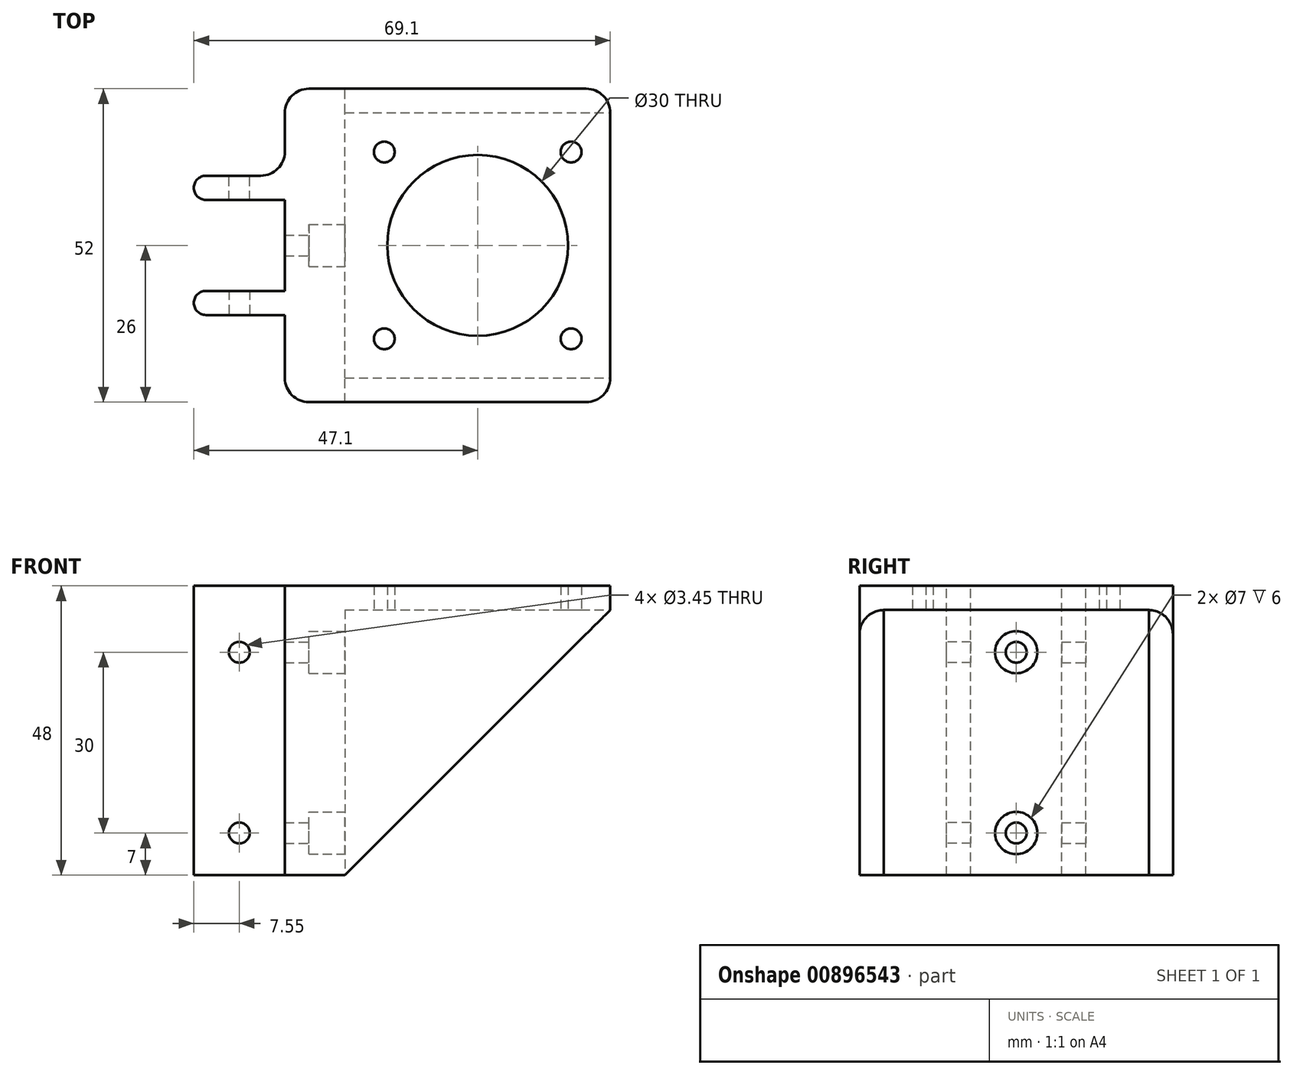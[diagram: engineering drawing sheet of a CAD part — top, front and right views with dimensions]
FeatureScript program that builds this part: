
annotation { "Feature Type Name" : "Feature", "Feature Type Description" : "" }
export const myFeature = defineFeature(function(context is Context, id is Id, definition is map)
    precondition{}
    {
        {
            var Q0;
            Q0=qCreatedBy(makeId("Top.planeOp"),FACE);
            var sketch = newSketch(context, id + "F0", { "sketchPlane" : qUnion([Q0])});
            skLineSegment(sketch, "E0.bottom", {"start": v(0, 0) * mm, "end": v(10, 0) * mm});
            skLineSegment(sketch, "E0.top", {"start": v(0, 52) * mm, "end": v(10, 52) * mm});
            skLineSegment(sketch, "E0.left", {"start": v(0, 0) * mm, "end": v(0, 52) * mm});
            skLineSegment(sketch, "E0.right", {"start": v(10, 0) * mm, "end": v(10, 52) * mm});
            skSolve(sketch);
        }
        {
            var Q0;
            Q0=qSketchRegion(id+"F0",true);
            extrude(context, id + "F1", {"entities" : qUnion([Q0]), "depth" : 44 * mm, "offsetDistance" : 25 * mm});
        }
        {
            var Q0;
            Q0=makeQuery(id+"F1.opExtrude","CAP_FACE",FACE,{"disambiguationData":[OSD([sQuery(id+"F0.wireOp",EDGE,"E0.bottom"),sQuery(id+"F0.wireOp",EDGE,"E0.top"),sQuery(id+"F0.wireOp",EDGE,"E0.left"),sQuery(id+"F0.wireOp",EDGE,"E0.right")])],"isStart":false});
            var sketch = newSketch(context, id + "F2", { "sketchPlane" : qUnion([Q0])});
            skLineSegment(sketch, "E1.bottom", {"start": v(0, 52) * mm, "end": v(54, 52) * mm});
            skLineSegment(sketch, "E1.top", {"start": v(0, 0) * mm, "end": v(54, 0) * mm});
            skLineSegment(sketch, "E1.left", {"start": v(0, 52) * mm, "end": v(0, 0) * mm});
            skLineSegment(sketch, "E1.right", {"start": v(54, 52) * mm, "end": v(54, 0) * mm});
            skSolve(sketch);
        }
        {
            var Q0;
            Q0=qSketchRegion(id+"F2",true);
            extrude(context, id + "F3", {"entities" : qUnion([Q0]), "operationType" : NewBodyOperationType.ADD, "depth" : 4 * mm, "offsetDistance" : 25 * mm});
        }
        {
            var Q0;
            Q0=makeQuery(id+"F3.boolean.opBoolean","MERGE",FACE,{"derivedFrom":[makeQuery(id+"F1.opExtrude","SWEPT_FACE",FACE,{"disambiguationData":[OSD([sQuery(id+"F0.wireOp",EDGE,"E0.bottom")])]}),makeQuery(id+"F3.opExtrude","SWEPT_FACE",FACE,{"disambiguationData":[OSD([sQuery(id+"F2.wireOp",EDGE,"E1.top")])]})]});
            var sketch = newSketch(context, id + "F4", { "sketchPlane" : qUnion([Q0])});
            skLineSegment(sketch, "E2", {"start": v(54, 44) * mm, "end": v(10, 0) * mm});
            skLineSegment(sketch, "E3", {"start": v(54, 44) * mm, "end": v(10, 44) * mm});
            skLineSegment(sketch, "E4", {"start": v(10, 44) * mm, "end": v(10, 0) * mm});
            skSolve(sketch);
        }
        {
            var Q0;
            Q0=qSketchRegion(id+"F4",true);
            extrude(context, id + "F5", {"entities" : qUnion([Q0]), "operationType" : NewBodyOperationType.ADD, "oppositeDirection" : true, "depth" : 4 * mm, "offsetDistance" : 25 * mm});
        }
        {
            var Q0;
            Q0=makeQuery(id+"F3.boolean.opBoolean","MERGE",FACE,{"derivedFrom":[makeQuery(id+"F1.opExtrude","SWEPT_FACE",FACE,{"disambiguationData":[OSD([sQuery(id+"F0.wireOp",EDGE,"E0.top")])]}),makeQuery(id+"F3.opExtrude","SWEPT_FACE",FACE,{"disambiguationData":[OSD([sQuery(id+"F2.wireOp",EDGE,"E1.bottom")])]})]});
            var sketch = newSketch(context, id + "F6", { "sketchPlane" : qUnion([Q0])});
            skLineSegment(sketch, "E5", {"start": v(-54, 44) * mm, "end": v(-10, 0) * mm});
            skLineSegment(sketch, "E6", {"start": v(-10, 0) * mm, "end": v(-10, 44) * mm});
            skLineSegment(sketch, "E7", {"start": v(-10, 44) * mm, "end": v(-54, 44) * mm});
            skSolve(sketch);
        }
        {
            var Q0;
            Q0=qSketchRegion(id+"F6",true);
            extrude(context, id + "F7", {"entities" : qUnion([Q0]), "operationType" : NewBodyOperationType.ADD, "oppositeDirection" : true, "depth" : 4 * mm, "offsetDistance" : 25 * mm});
        }
        {
            var Q0;
            Q0=makeQuery(id+"F3.opExtrude","CAP_FACE",FACE,{"disambiguationData":[OSD([sQuery(id+"F2.wireOp",EDGE,"E1.bottom"),sQuery(id+"F2.wireOp",EDGE,"E1.top"),sQuery(id+"F2.wireOp",EDGE,"E1.left"),sQuery(id+"F2.wireOp",EDGE,"E1.right")])],"isStart":true});
            var sketch = newSketch(context, id + "F8", { "sketchPlane" : qUnion([Q0])});
            skLineSegment(sketch, "E8", {"start": v(32, -48) * mm, "end": v(32, -26) * mm, "construction": true});
            skLineSegment(sketch, "E9", {"start": v(32, -26) * mm, "end": v(54, -26) * mm, "construction": true});
            skCircle(sketch, "E10", {"center": v(32, -26) * mm, "radius": 15 * mm});
            skLineSegment(sketch, "E11.bottom", {"start": v(16.5, -10.5) * mm, "end": v(47.5, -10.5) * mm, "construction": true});
            skLineSegment(sketch, "E11.top", {"start": v(16.5, -41.5) * mm, "end": v(47.5, -41.5) * mm, "construction": true});
            skLineSegment(sketch, "E11.left", {"start": v(16.5, -10.5) * mm, "end": v(16.5, -41.5) * mm, "construction": true});
            skLineSegment(sketch, "E11.right", {"start": v(47.5, -10.5) * mm, "end": v(47.5, -41.5) * mm, "construction": true});
            skCircle(sketch, "E12", {"center": v(16.5, -10.5) * mm, "radius": 1.73 * mm});
            skCircle(sketch, "E13", {"center": v(47.5, -10.5) * mm, "radius": 1.73 * mm});
            skCircle(sketch, "E14", {"center": v(47.5, -41.5) * mm, "radius": 1.73 * mm});
            skCircle(sketch, "E15", {"center": v(16.5, -41.5) * mm, "radius": 1.73 * mm});
            skSolve(sketch);
        }
        {
            var Q0;
            Q0=qSketchRegion(id+"F8",true);
            extrude(context, id + "F9", {"entities" : qUnion([Q0]), "operationType" : NewBodyOperationType.REMOVE, "endBound" : BoundingType.UP_TO_NEXT, "oppositeDirection" : true, "depth" : 2 * mm, "offsetDistance" : 25 * mm});
        }
        {
            var Q0;
            Q0=makeQuery(id+"F1.opExtrude","SWEPT_FACE",FACE,{"disambiguationData":[OSD([sQuery(id+"F0.wireOp",EDGE,"E0.right")])]});
            var sketch = newSketch(context, id + "F10", { "sketchPlane" : qUnion([Q0])});
            skLineSegment(sketch, "E16", {"start": v(26, 44) * mm, "end": v(26, 37) * mm, "construction": true});
            skCircle(sketch, "E17", {"center": v(26, 37) * mm, "radius": 1.73 * mm});
            skCircle(sketch, "E18", {"center": v(26, 7) * mm, "radius": 1.73 * mm});
            skCircle(sketch, "E19", {"center": v(26, 37) * mm, "radius": 3.5 * mm});
            skCircle(sketch, "E20", {"center": v(26, 7) * mm, "radius": 3.5 * mm});
            skLineSegment(sketch, "E21", {"start": v(26, 0) * mm, "end": v(26, 7) * mm, "construction": true});
            skSolve(sketch);
        }
        {
            var Q0;
            Q0=makeQuery(id+"F10.imprint","IMPRINT",FACE,{"disambiguationData":[TD([[makeQuery(id+"F10.imprint","IMPRINT",EDGE,{"derivedFrom":sQuery(id+"F10.wireOp",EDGE,"E17")}),1.0]])]});
            var Q1;
            Q1=makeQuery(id+"F10.imprint","IMPRINT",FACE,{"disambiguationData":[TD([[makeQuery(id+"F10.imprint","IMPRINT",EDGE,{"derivedFrom":sQuery(id+"F10.wireOp",EDGE,"4CqJ4LeS-7kQp-3Y7h-jtAy-PQuo6a8Fykjg")}),1.0]])]});
            var Q2;
            Q2=makeQuery(id+"F10.imprint","IMPRINT",FACE,{"disambiguationData":[TD([[makeQuery(id+"F10.imprint","IMPRINT",EDGE,{"derivedFrom":sQuery(id+"F10.wireOp",EDGE,"PDHdAQvy-AfDD-QxQ9-jLki-7bYX29yO74vW")}),1.0]])]});
            var Q3;
            Q3=makeQuery(id+"F10.imprint","IMPRINT",FACE,{"disambiguationData":[TD([[makeQuery(id+"F10.imprint","IMPRINT",EDGE,{"derivedFrom":sQuery(id+"F10.wireOp",EDGE,"E18")}),1.0]])]});
            extrude(context, id + "F11", {"entities" : qUnion([Q0, Q1, Q2, Q3]), "operationType" : NewBodyOperationType.REMOVE, "oppositeDirection" : true, "depth" : 10 * mm, "offsetDistance" : 25 * mm});
        }
        {
            var Q0;
            Q0=qSketchRegion(id+"F10",true);
            extrude(context, id + "F12", {"entities" : qUnion([Q0]), "operationType" : NewBodyOperationType.REMOVE, "oppositeDirection" : true, "depth" : 6 * mm, "offsetDistance" : 25 * mm});
        }
        {
            var Q0;
            Q0=makeQuery(id+"F3.boolean.opBoolean","MERGE",EDGE,{"derivedFrom":[makeQuery(id+"F1.opExtrude","SWEPT_EDGE",EDGE,{"disambiguationData":[OSD([sQuery(id+"F0.wireOp",EDGE,"E0.bottom"),sQuery(id+"F0.wireOp",EDGE,"E0.left")])]}),makeQuery(id+"F3.opExtrude","SWEPT_EDGE",EDGE,{"disambiguationData":[OSD([sQuery(id+"F2.wireOp",EDGE,"E1.top"),sQuery(id+"F2.wireOp",EDGE,"E1.left")])]})]});
            var Q1;
            Q1=makeQuery(id+"F3.boolean.opBoolean","MERGE",EDGE,{"derivedFrom":[makeQuery(id+"F1.opExtrude","SWEPT_EDGE",EDGE,{"disambiguationData":[OSD([sQuery(id+"F0.wireOp",EDGE,"E0.top"),sQuery(id+"F0.wireOp",EDGE,"E0.left")])]}),makeQuery(id+"F3.opExtrude","SWEPT_EDGE",EDGE,{"disambiguationData":[OSD([sQuery(id+"F2.wireOp",EDGE,"E1.bottom"),sQuery(id+"F2.wireOp",EDGE,"E1.left")])]})]});
            var Q2;
            Q2=makeQuery(id+"F3.opExtrude","SWEPT_EDGE",EDGE,{"disambiguationData":[OSD([sQuery(id+"F2.wireOp",EDGE,"E1.bottom"),sQuery(id+"F2.wireOp",EDGE,"E1.right")])]});
            var Q3;
            Q3=makeQuery(id+"F3.opExtrude","SWEPT_EDGE",EDGE,{"disambiguationData":[OSD([sQuery(id+"F2.wireOp",EDGE,"E1.top"),sQuery(id+"F2.wireOp",EDGE,"E1.right")])]});
            fillet(context, id + "F13", {"entities" : qUnion([Q0, Q1, Q2, Q3]), "radius" : 4 * mm, "tangentPropagation" : true, "allowEdgeOverflow" : false});
        }
        {
            var Q0;
            Q0=makeQuery(id+"F3.opExtrude","CAP_FACE",FACE,{"disambiguationData":[OSD([sQuery(id+"F2.wireOp",EDGE,"E1.bottom"),sQuery(id+"F2.wireOp",EDGE,"E1.top"),sQuery(id+"F2.wireOp",EDGE,"E1.left"),sQuery(id+"F2.wireOp",EDGE,"E1.right")])],"isStart":false});
            var sketch = newSketch(context, id + "F14", { "sketchPlane" : qUnion([Q0])});
            skLineSegment(sketch, "E22.bottom", {"start": v(-15.1, 33.55) * mm, "end": v(0, 33.55) * mm, "construction": true});
            skLineSegment(sketch, "E22.top", {"start": v(-15.1, 18.45) * mm, "end": v(0, 18.45) * mm, "construction": true});
            skLineSegment(sketch, "E22.left", {"start": v(-15.1, 33.55) * mm, "end": v(-15.1, 18.45) * mm, "construction": true});
            skLineSegment(sketch, "E22.right", {"start": v(0, 33.55) * mm, "end": v(0, 18.45) * mm, "construction": true});
            skPoint(sketch, "E23", {"position": v(0, 26) * mm});
            skLineSegment(sketch, "E24.bottom", {"start": v(0, 33.55) * mm, "end": v(-15.1, 33.55) * mm});
            skLineSegment(sketch, "E24.top", {"start": v(0, 37.55) * mm, "end": v(-15.1, 37.55) * mm});
            skLineSegment(sketch, "E24.left", {"start": v(0, 33.55) * mm, "end": v(0, 37.55) * mm});
            skLineSegment(sketch, "E24.right", {"start": v(-15.1, 33.55) * mm, "end": v(-15.1, 37.55) * mm});
            skLineSegment(sketch, "E25.bottom", {"start": v(0, 18.45) * mm, "end": v(-15.1, 18.45) * mm});
            skLineSegment(sketch, "E25.top", {"start": v(0, 14.45) * mm, "end": v(-15.1, 14.45) * mm});
            skLineSegment(sketch, "E25.left", {"start": v(0, 18.45) * mm, "end": v(0, 14.45) * mm});
            skLineSegment(sketch, "E25.right", {"start": v(-15.1, 18.45) * mm, "end": v(-15.1, 14.45) * mm});
            skSolve(sketch);
        }
        {
            var Q0;
            Q0 = qSketchRegion(id + "F14", true);
            extrude(context, id + "F15", {"entities" : qUnion([Q0]), "operationType" : NewBodyOperationType.ADD, "oppositeDirection" : true, "depth" : 48 * mm, "offsetDistance" : 25 * mm});
        }
        {
            var Q0;
            Q0=makeQuery(id+"F15.opExtrude","SWEPT_FACE",FACE,{"disambiguationData":[OSD([sQuery(id+"F14.wireOp",EDGE,"E25.top")])]});
            var sketch = newSketch(context, id + "F16", { "sketchPlane" : qUnion([Q0])});
            skLineSegment(sketch, "E26", {"start": v(-7.55, 48) * mm, "end": v(-7.55, 37) * mm, "construction": true});
            skLineSegment(sketch, "E27", {"start": v(-7.55, 0) * mm, "end": v(-7.55, 7) * mm, "construction": true});
            skCircle(sketch, "E28", {"center": v(-7.55, 7) * mm, "radius": 1.73 * mm});
            skCircle(sketch, "E29", {"center": v(-7.55, 7) * mm, "radius": 3.5 * mm});
            skCircle(sketch, "E30", {"center": v(-7.55, 37) * mm, "radius": 1.73 * mm});
            skCircle(sketch, "E31", {"center": v(-7.55, 37) * mm, "radius": 3.5 * mm});
            skSolve(sketch);
        }
        {
            var Q0;
            Q0=makeQuery(id+"F16.imprint","IMPRINT",FACE,{"disambiguationData":[TD([[makeQuery(id+"F16.imprint","IMPRINT",EDGE,{"derivedFrom":sQuery(id+"F16.wireOp",EDGE,"E30")}),1.0]])]});
            var Q1;
            Q1=makeQuery(id+"F16.imprint","IMPRINT",FACE,{"disambiguationData":[TD([[makeQuery(id+"F16.imprint","IMPRINT",EDGE,{"derivedFrom":sQuery(id+"F16.wireOp",EDGE,"E28")}),1.0]])]});
            extrude(context, id + "F17", {"entities" : qUnion([Q0, Q1]), "operationType" : NewBodyOperationType.REMOVE, "endBound" : BoundingType.UP_TO_NEXT, "oppositeDirection" : true, "depth" : 25 * mm, "offsetDistance" : 25 * mm});
        }
        {
            var Q0;
            Q0=makeQuery(id+"F15.opExtrude","SWEPT_FACE",FACE,{"disambiguationData":[OSD([sQuery(id+"F14.wireOp",EDGE,"E24.top")])]});
            var sketch = newSketch(context, id + "F18", { "sketchPlane" : qUnion([Q0])});
            skLineSegment(sketch, "E32", {"start": v(7.55, 48) * mm, "end": v(7.55, 37) * mm, "construction": true});
            skLineSegment(sketch, "E33", {"start": v(7.55, 0) * mm, "end": v(7.55, 7) * mm, "construction": true});
            skCircle(sketch, "E34", {"center": v(7.55, 37) * mm, "radius": 1.73 * mm});
            skCircle(sketch, "E35", {"center": v(7.55, 37) * mm, "radius": 3.5 * mm});
            skCircle(sketch, "E36", {"center": v(7.55, 7) * mm, "radius": 1.73 * mm});
            skCircle(sketch, "E37", {"center": v(7.55, 7) * mm, "radius": 3.5 * mm});
            skSolve(sketch);
        }
        {
            var Q0;
            Q0=makeQuery(id+"F18.imprint","IMPRINT",FACE,{"disambiguationData":[TD([[makeQuery(id+"F18.imprint","IMPRINT",EDGE,{"derivedFrom":sQuery(id+"F18.wireOp",EDGE,"E34")}),1.0]])]});
            var Q1;
            Q1=makeQuery(id+"F18.imprint","IMPRINT",FACE,{"disambiguationData":[TD([[makeQuery(id+"F18.imprint","IMPRINT",EDGE,{"derivedFrom":sQuery(id+"F18.wireOp",EDGE,"E36")}),1.0]])]});
            extrude(context, id + "F19", {"entities" : qUnion([Q0, Q1]), "operationType" : NewBodyOperationType.REMOVE, "endBound" : BoundingType.UP_TO_NEXT, "oppositeDirection" : true, "depth" : 25 * mm, "offsetDistance" : 25 * mm});
        }
        {
            var Q0;
            Q0=makeQuery(id+"F15.opExtrude","SWEPT_EDGE",EDGE,{"disambiguationData":[OSD([sQuery(id+"F2.wireOp",EDGE,"E1.left"),sQuery(id+"F14.wireOp",EDGE,"E25.top"),sQuery(id+"F14.wireOp",EDGE,"E25.left")])]});
            var Q1;
            Q1=makeQuery(id+"F15.opExtrude","SWEPT_EDGE",EDGE,{"disambiguationData":[OSD([sQuery(id+"F2.wireOp",EDGE,"E1.left"),sQuery(id+"F14.wireOp",EDGE,"E24.top"),sQuery(id+"F14.wireOp",EDGE,"E24.left")])]});
            fillet(context, id + "F20", {"entities" : qUnion([Q0, Q1]), "radius" : 4 * mm, "tangentPropagation" : true, "allowEdgeOverflow" : false});
        }
        {
            var Q0;
            Q0=makeQuery(id+"F15.opExtrude","SWEPT_EDGE",EDGE,{"disambiguationData":[OSD([sQuery(id+"F14.wireOp",EDGE,"E24.top"),sQuery(id+"F14.wireOp",EDGE,"E24.right")])]});
            var Q1;
            Q1=makeQuery(id+"F15.opExtrude","SWEPT_EDGE",EDGE,{"disambiguationData":[OSD([sQuery(id+"F14.wireOp",EDGE,"E24.bottom"),sQuery(id+"F14.wireOp",EDGE,"E24.right")])]});
            var Q2;
            Q2=makeQuery(id+"F15.opExtrude","SWEPT_EDGE",EDGE,{"disambiguationData":[OSD([sQuery(id+"F14.wireOp",EDGE,"E25.bottom"),sQuery(id+"F14.wireOp",EDGE,"E25.right")])]});
            var Q3;
            Q3=makeQuery(id+"F15.opExtrude","SWEPT_EDGE",EDGE,{"disambiguationData":[OSD([sQuery(id+"F14.wireOp",EDGE,"E25.top"),sQuery(id+"F14.wireOp",EDGE,"E25.right")])]});
            fillet(context, id + "F21", {"entities" : qUnion([Q0, Q1, Q2, Q3]), "radius" : 2 * mm, "tangentPropagation" : true, "allowEdgeOverflow" : false});
        }
    });
